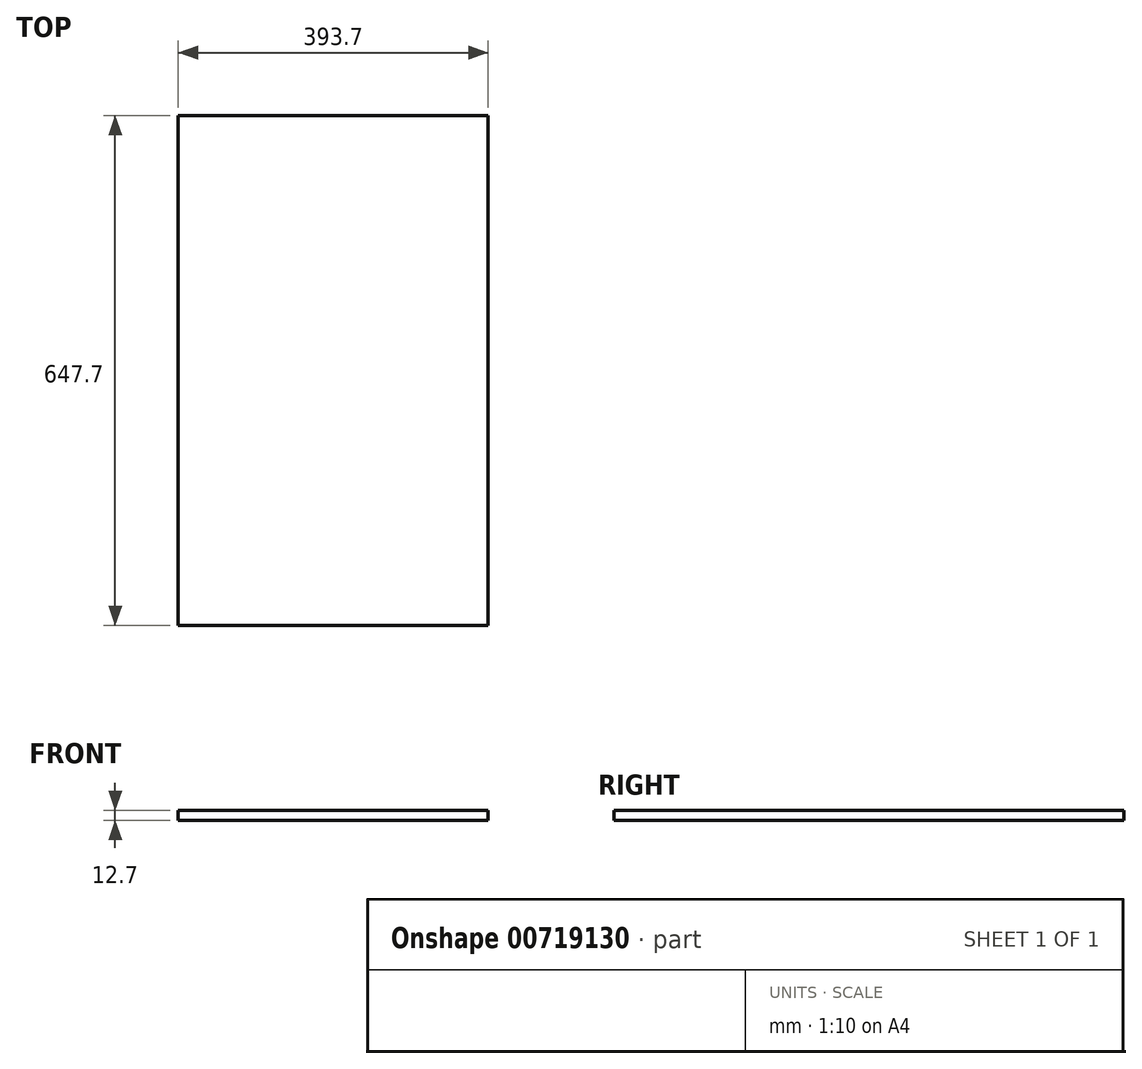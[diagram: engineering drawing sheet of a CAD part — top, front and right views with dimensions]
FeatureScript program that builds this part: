
annotation { "Feature Type Name" : "Feature", "Feature Type Description" : "" }
export const myFeature = defineFeature(function(context is Context, id is Id, definition is map)
    precondition{}
    {
        {
            var Q0;
            Q0=qCreatedBy(makeId("Top.planeOp"),FACE);
            var sketch = newSketch(context, id + "F0", { "sketchPlane" : qUnion([Q0])});
            skLineSegment(sketch, "E0.bottom", {"start": v(0, 0) * mm, "end": v(-393.7, 0) * mm});
            skLineSegment(sketch, "E0.top", {"start": v(0, 647.7) * mm, "end": v(-393.7, 647.7) * mm});
            skLineSegment(sketch, "E0.left", {"start": v(0, 0) * mm, "end": v(0, 647.7) * mm});
            skLineSegment(sketch, "E0.right", {"start": v(-393.7, 0) * mm, "end": v(-393.7, 647.7) * mm});
            skSolve(sketch);
        }
        {
            var Q0;
            Q0 = qSketchRegion(id + "F0", true);
            extrude(context, id + "F1", {"entities" : qUnion([Q0]), "depth" : 12.7 * mm, "offsetDistance" : 25.4 * mm});
        }
    });
